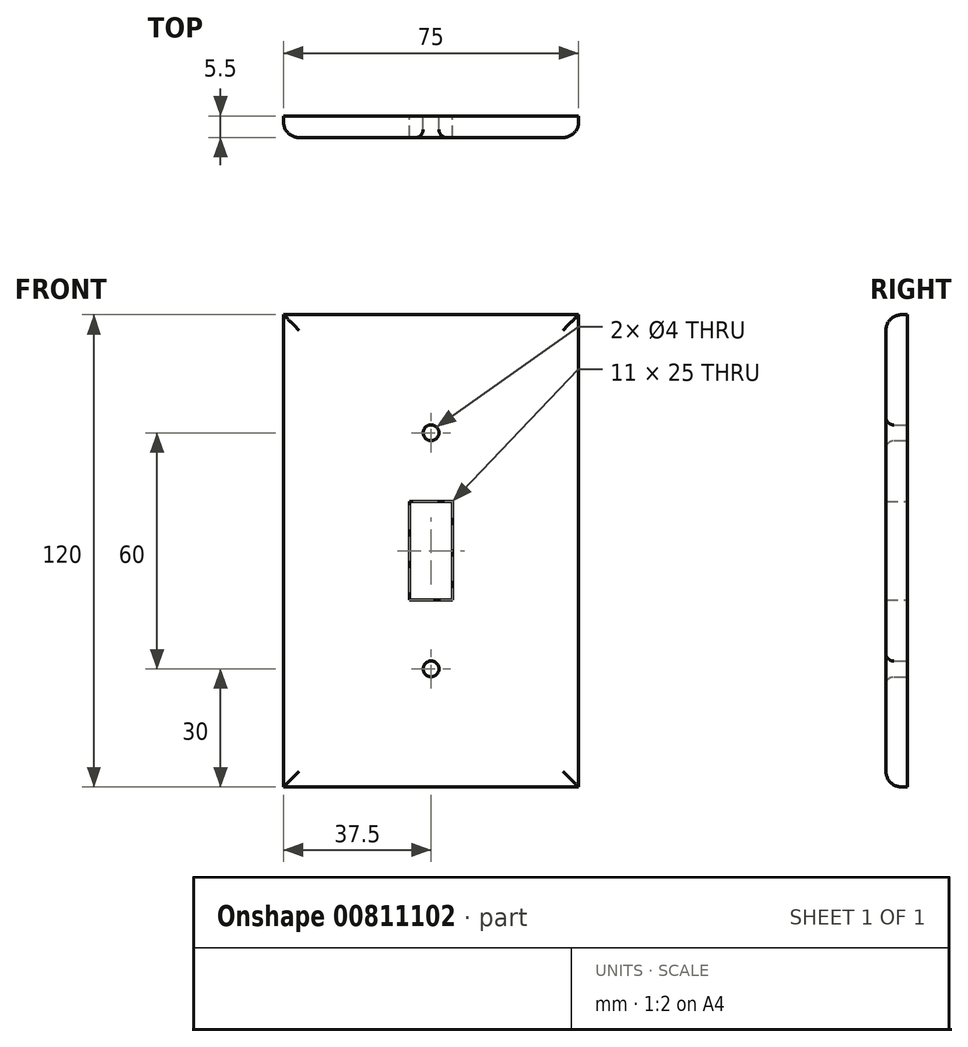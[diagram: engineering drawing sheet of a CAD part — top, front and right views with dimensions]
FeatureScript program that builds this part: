
annotation { "Feature Type Name" : "Feature", "Feature Type Description" : "" }
export const myFeature = defineFeature(function(context is Context, id is Id, definition is map)
    precondition{}
    {
        {
            var Q0;
            Q0=qCreatedBy(makeId("Front.planeOp"),FACE);
            var sketch = newSketch(context, id + "F0", { "sketchPlane" : qUnion([Q0])});
            skLineSegment(sketch, "E0.bottom", {"start": v(37.5, 60) * mm, "end": v(-37.5, 60) * mm});
            skLineSegment(sketch, "E0.top", {"start": v(37.5, -60) * mm, "end": v(-37.5, -60) * mm});
            skLineSegment(sketch, "E0.left", {"start": v(37.5, 60) * mm, "end": v(37.5, -60) * mm});
            skLineSegment(sketch, "E0.right", {"start": v(-37.5, 60) * mm, "end": v(-37.5, -60) * mm});
            skPoint(sketch, "E0.middle", {"position": v(0, 0) * mm});
            skLineSegment(sketch, "E1.bottom", {"start": v(5.5, 12.5) * mm, "end": v(-5.5, 12.5) * mm});
            skLineSegment(sketch, "E1.top", {"start": v(5.5, -12.5) * mm, "end": v(-5.5, -12.5) * mm});
            skLineSegment(sketch, "E1.left", {"start": v(5.5, 12.5) * mm, "end": v(5.5, -12.5) * mm});
            skLineSegment(sketch, "E1.right", {"start": v(-5.5, 12.5) * mm, "end": v(-5.5, -12.5) * mm});
            skCircle(sketch, "E2", {"center": v(0, -30) * mm, "radius": 2 * mm});
            skPoint(sketch, "E3.centerSnap0", {"position": v(0, -12.5) * mm});
            skCircle(sketch, "E4", {"center": v(0, 30) * mm, "radius": 2 * mm});
            skSolve(sketch);
        }
        {
            var Q0;
            Q0 = qSketchRegion(id + "F0", true);
            extrude(context, id + "F1", {"entities" : qUnion([Q0]), "depth" : 5.5 * mm, "offsetDistance" : 25 * mm});
        }
        {
            var Q0;
            Q0=makeQuery(id+"F1.opExtrude","CAP_EDGE",EDGE,{"disambiguationData":[OSD([sQuery(id+"F0.wireOp",EDGE,"E0.right")])],"isStart":false});
            var Q1;
            Q1=makeQuery(id+"F1.opExtrude","CAP_EDGE",EDGE,{"disambiguationData":[OSD([sQuery(id+"F0.wireOp",EDGE,"E0.bottom")])],"isStart":false});
            var Q2;
            Q2=makeQuery(id+"F1.opExtrude","CAP_EDGE",EDGE,{"disambiguationData":[OSD([sQuery(id+"F0.wireOp",EDGE,"E0.left")])],"isStart":false});
            var Q3;
            Q3=makeQuery(id+"F1.opExtrude","CAP_EDGE",EDGE,{"disambiguationData":[OSD([sQuery(id+"F0.wireOp",EDGE,"E0.top")])],"isStart":false});
            fillet(context, id + "F2", {"entities" : qUnion([Q0, Q1, Q2, Q3]), "radius" : 4 * mm, "tangentPropagation" : true, "allowEdgeOverflow" : false});
        }
        {
            var Q0;
            Q0=makeQuery(id+"F1.opExtrude","CAP_EDGE",EDGE,{"disambiguationData":[OSD([sQuery(id+"F0.wireOp",EDGE,"E4")])],"isStart":false});
            var Q1;
            Q1=makeQuery(id+"F1.opExtrude","CAP_EDGE",EDGE,{"disambiguationData":[OSD([sQuery(id+"F0.wireOp",EDGE,"E2")])],"isStart":false});
            fillet(context, id + "F3", {"entities" : qUnion([Q0, Q1]), "radius" : 2 * mm, "tangentPropagation" : true, "allowEdgeOverflow" : false});
        }
    });
